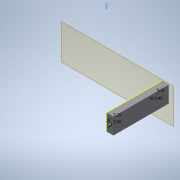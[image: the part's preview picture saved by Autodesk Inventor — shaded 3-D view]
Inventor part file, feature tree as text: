
AUTODESK INVENTOR PART (.ipt)
format: ipt  version: 2020 (Build 240168000, 168)  size: 147,968 bytes
history: native  units: mm
features: other x6, extrude x4, sketch x4, reference x2, projected_geometry x1
ambient origin geometry x8: Origin, YZ Plane, XZ Plane, XY Plane, X Axis, Y Axis, Z Axis, Center Point
bodies: Body1 (feature_tree)
feature tree (17):
  other  "Bryła1"
  other  "Płaszczyzna konstrukcyjna1"
  extrude  "Wyciągnięcie proste1"  Depth=76.0mm TaperAngle=0.0deg
  sketch  "Szkic2"
  extrude  "Wyciągnięcie proste3"  Depth=10.0mm
  extrude  "Wyciągnięcie proste4"  Depth=10.0mm
  extrude  "Wyciągnięcie proste2"  Depth=3.5mm
  sketch  "Szkic1"
  reference  "Odniesienie1"
  reference  "Odniesienie2"
  sketch  "Szkic3"
  sketch  "Szkic4"
  projected_geometry  "Pętla rzutowana1"
  other  "<userpath>\Desktop\3d\scanning-robot\Assembly1.iam"
  other  "Assembly1.iam"
  other  "base:1"
  other  "wheel-adapter:1"
